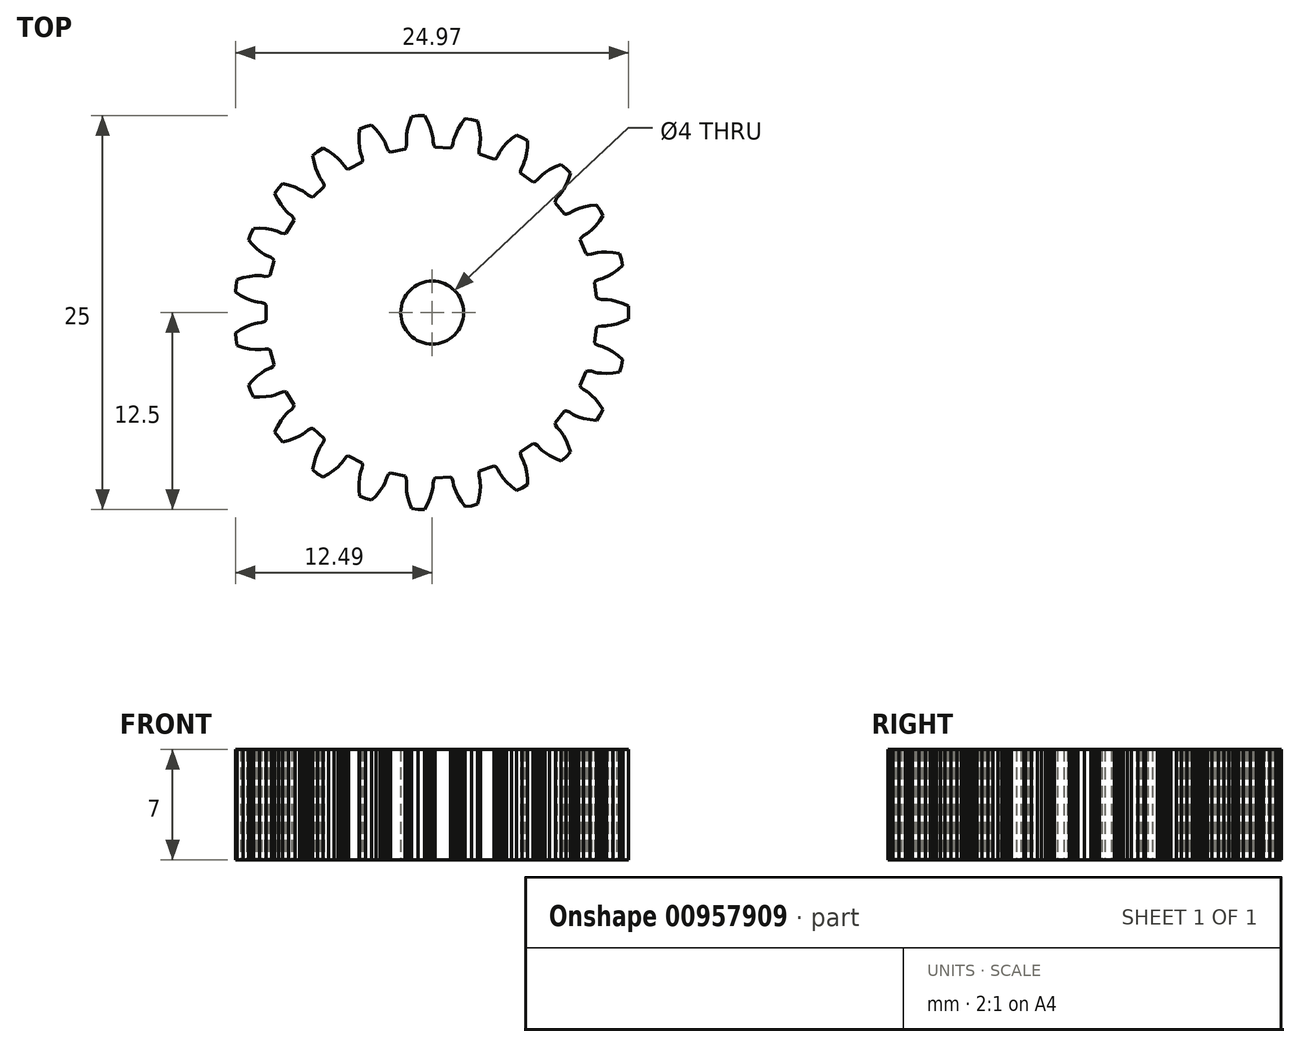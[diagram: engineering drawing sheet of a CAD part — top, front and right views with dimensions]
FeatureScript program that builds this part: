
annotation { "Feature Type Name" : "Feature", "Feature Type Description" : "" }
export const myFeature = defineFeature(function(context is Context, id is Id, definition is map)
    precondition{}
    {
        {
            var Q0;
            Q0=qCreatedBy(makeId("Top.planeOp"),FACE);
            var sketch = newSketch(context, id + "F0", { "sketchPlane" : qUnion([Q0])});
            skLineSegment(sketch, "E0", {"start": v(11.88, -3.76) * mm, "end": v(12.02, -3.38) * mm});
            skLineSegment(sketch, "E1", {"start": v(12.02, -3.38) * mm, "end": v(12.1, -2.98) * mm});
            skLineSegment(sketch, "E2", {"start": v(12.1, -2.98) * mm, "end": v(11.8, -2.73) * mm});
            skLineSegment(sketch, "E3", {"start": v(11.8, -2.73) * mm, "end": v(11.46, -2.48) * mm});
            skLineSegment(sketch, "E4", {"start": v(11.46, -2.48) * mm, "end": v(11.17, -2.32) * mm});
            skLineSegment(sketch, "E5", {"start": v(11.17, -2.32) * mm, "end": v(10.95, -2.22) * mm});
            skLineSegment(sketch, "E6", {"start": v(10.95, -2.22) * mm, "end": v(10.81, -2.17) * mm});
            skLineSegment(sketch, "E7", {"start": v(10.81, -2.17) * mm, "end": v(10.56, -2.1) * mm});
            skLineSegment(sketch, "E8", {"start": v(10.56, -2.1) * mm, "end": v(10.38, -2) * mm});
            skLineSegment(sketch, "E9", {"start": v(10.38, -2) * mm, "end": v(10.3, -1.9) * mm});
            skLineSegment(sketch, "E10", {"start": v(10.3, -1.9) * mm, "end": v(10.42, -0.95) * mm});
            skLineSegment(sketch, "E11", {"start": v(10.42, -0.95) * mm, "end": v(10.53, -0.88) * mm});
            skLineSegment(sketch, "E12", {"start": v(10.53, -0.88) * mm, "end": v(10.74, -0.84) * mm});
            skLineSegment(sketch, "E13", {"start": v(10.74, -0.84) * mm, "end": v(11, -0.85) * mm});
            skLineSegment(sketch, "E14", {"start": v(11, -0.85) * mm, "end": v(11.14, -0.83) * mm});
            skLineSegment(sketch, "E15", {"start": v(11.14, -0.83) * mm, "end": v(11.38, -0.8) * mm});
            skLineSegment(sketch, "E16", {"start": v(11.38, -0.8) * mm, "end": v(11.7, -0.71) * mm});
            skLineSegment(sketch, "E17", {"start": v(11.7, -0.71) * mm, "end": v(12.1, -0.57) * mm});
            skLineSegment(sketch, "E18", {"start": v(12.1, -0.57) * mm, "end": v(12.45, -0.4) * mm});
            skLineSegment(sketch, "E19", {"start": v(12.45, -0.4) * mm, "end": v(12.48, 0) * mm});
            skLineSegment(sketch, "E20", {"start": v(12.48, 0) * mm, "end": v(12.45, 0.4) * mm});
            skLineSegment(sketch, "E21", {"start": v(12.45, 0.4) * mm, "end": v(12.1, 0.57) * mm});
            skLineSegment(sketch, "E22", {"start": v(12.1, 0.57) * mm, "end": v(11.7, 0.71) * mm});
            skLineSegment(sketch, "E23", {"start": v(11.7, 0.71) * mm, "end": v(11.38, 0.8) * mm});
            skLineSegment(sketch, "E24", {"start": v(11.38, 0.8) * mm, "end": v(11.14, 0.83) * mm});
            skLineSegment(sketch, "E25", {"start": v(11.14, 0.83) * mm, "end": v(11, 0.85) * mm});
            skLineSegment(sketch, "E26", {"start": v(11, 0.85) * mm, "end": v(10.74, 0.84) * mm});
            skLineSegment(sketch, "E27", {"start": v(10.74, 0.84) * mm, "end": v(10.53, 0.88) * mm});
            skLineSegment(sketch, "E28", {"start": v(10.53, 0.88) * mm, "end": v(10.42, 0.95) * mm});
            skLineSegment(sketch, "E29", {"start": v(10.42, 0.95) * mm, "end": v(10.3, 1.9) * mm});
            skLineSegment(sketch, "E30", {"start": v(10.3, 1.9) * mm, "end": v(10.38, 2) * mm});
            skLineSegment(sketch, "E31", {"start": v(10.38, 2) * mm, "end": v(10.56, 2.1) * mm});
            skLineSegment(sketch, "E32", {"start": v(10.56, 2.1) * mm, "end": v(10.81, 2.17) * mm});
            skLineSegment(sketch, "E33", {"start": v(10.81, 2.17) * mm, "end": v(10.95, 2.22) * mm});
            skLineSegment(sketch, "E34", {"start": v(10.95, 2.22) * mm, "end": v(11.17, 2.32) * mm});
            skLineSegment(sketch, "E35", {"start": v(11.17, 2.32) * mm, "end": v(11.46, 2.48) * mm});
            skLineSegment(sketch, "E36", {"start": v(11.46, 2.48) * mm, "end": v(11.8, 2.73) * mm});
            skLineSegment(sketch, "E37", {"start": v(11.8, 2.73) * mm, "end": v(12.1, 2.98) * mm});
            skLineSegment(sketch, "E38", {"start": v(12.02, 3.38) * mm, "end": v(11.88, 3.76) * mm});
            skLineSegment(sketch, "E39", {"start": v(11.88, 3.76) * mm, "end": v(11.5, 3.83) * mm});
            skLineSegment(sketch, "E40", {"start": v(11.5, 3.83) * mm, "end": v(11.08, 3.86) * mm});
            skLineSegment(sketch, "E41", {"start": v(11.08, 3.86) * mm, "end": v(10.74, 3.85) * mm});
            skLineSegment(sketch, "E42", {"start": v(10.74, 3.85) * mm, "end": v(10.5, 3.82) * mm});
            skLineSegment(sketch, "E43", {"start": v(10.5, 3.82) * mm, "end": v(10.36, 3.8) * mm});
            skLineSegment(sketch, "E44", {"start": v(10.36, 3.8) * mm, "end": v(10.11, 3.72) * mm});
            skLineSegment(sketch, "E45", {"start": v(10.11, 3.72) * mm, "end": v(9.9, 3.7) * mm});
            skLineSegment(sketch, "E46", {"start": v(9.9, 3.7) * mm, "end": v(9.78, 3.74) * mm});
            skLineSegment(sketch, "E47", {"start": v(9.78, 3.74) * mm, "end": v(9.4, 4.63) * mm});
            skLineSegment(sketch, "E48", {"start": v(9.4, 4.63) * mm, "end": v(9.45, 4.75) * mm});
            skLineSegment(sketch, "E49", {"start": v(9.45, 4.75) * mm, "end": v(9.6, 4.89) * mm});
            skLineSegment(sketch, "E50", {"start": v(9.6, 4.89) * mm, "end": v(9.83, 5.02) * mm});
            skLineSegment(sketch, "E51", {"start": v(9.83, 5.02) * mm, "end": v(9.95, 5.1) * mm});
            skLineSegment(sketch, "E52", {"start": v(9.95, 5.1) * mm, "end": v(10.13, 5.26) * mm});
            skLineSegment(sketch, "E53", {"start": v(10.13, 5.26) * mm, "end": v(10.36, 5.5) * mm});
            skLineSegment(sketch, "E54", {"start": v(10.36, 5.5) * mm, "end": v(10.63, 5.83) * mm});
            skLineSegment(sketch, "E55", {"start": v(10.63, 5.83) * mm, "end": v(10.84, 6.15) * mm});
            skLineSegment(sketch, "E56", {"start": v(10.84, 6.15) * mm, "end": v(10.66, 6.5) * mm});
            skLineSegment(sketch, "E57", {"start": v(10.66, 6.5) * mm, "end": v(10.42, 6.84) * mm});
            skLineSegment(sketch, "E58", {"start": v(10.42, 6.84) * mm, "end": v(10.04, 6.8) * mm});
            skLineSegment(sketch, "E59", {"start": v(10.04, 6.8) * mm, "end": v(9.62, 6.71) * mm});
            skLineSegment(sketch, "E60", {"start": v(9.62, 6.71) * mm, "end": v(9.3, 6.62) * mm});
            skLineSegment(sketch, "E61", {"start": v(9.3, 6.62) * mm, "end": v(9.08, 6.53) * mm});
            skLineSegment(sketch, "E62", {"start": v(9.08, 6.53) * mm, "end": v(8.95, 6.46) * mm});
            skLineSegment(sketch, "E63", {"start": v(8.95, 6.46) * mm, "end": v(8.73, 6.32) * mm});
            skLineSegment(sketch, "E64", {"start": v(8.73, 6.32) * mm, "end": v(8.53, 6.25) * mm});
            skLineSegment(sketch, "E65", {"start": v(8.53, 6.25) * mm, "end": v(8.4, 6.26) * mm});
            skLineSegment(sketch, "E66", {"start": v(8.4, 6.26) * mm, "end": v(7.8, 7) * mm});
            skLineSegment(sketch, "E67", {"start": v(7.8, 7) * mm, "end": v(7.82, 7.13) * mm});
            skLineSegment(sketch, "E68", {"start": v(7.82, 7.13) * mm, "end": v(7.93, 7.3) * mm});
            skLineSegment(sketch, "E69", {"start": v(7.93, 7.3) * mm, "end": v(8.1, 7.5) * mm});
            skLineSegment(sketch, "E70", {"start": v(8.1, 7.5) * mm, "end": v(8.2, 7.6) * mm});
            skLineSegment(sketch, "E71", {"start": v(8.2, 7.6) * mm, "end": v(8.34, 7.81) * mm});
            skLineSegment(sketch, "E72", {"start": v(8.34, 7.81) * mm, "end": v(8.5, 8.1) * mm});
            skLineSegment(sketch, "E73", {"start": v(8.5, 8.1) * mm, "end": v(8.66, 8.5) * mm});
            skLineSegment(sketch, "E74", {"start": v(8.66, 8.5) * mm, "end": v(8.78, 8.86) * mm});
            skLineSegment(sketch, "E75", {"start": v(8.78, 8.86) * mm, "end": v(8.5, 9.16) * mm});
            skLineSegment(sketch, "E76", {"start": v(8.5, 9.16) * mm, "end": v(8.19, 9.41) * mm});
            skLineSegment(sketch, "E77", {"start": v(8.19, 9.41) * mm, "end": v(7.83, 9.27) * mm});
            skLineSegment(sketch, "E78", {"start": v(7.83, 9.27) * mm, "end": v(7.45, 9.07) * mm});
            skLineSegment(sketch, "E79", {"start": v(7.45, 9.07) * mm, "end": v(7.17, 8.9) * mm});
            skLineSegment(sketch, "E80", {"start": v(7.17, 8.9) * mm, "end": v(6.98, 8.75) * mm});
            skLineSegment(sketch, "E81", {"start": v(6.98, 8.75) * mm, "end": v(6.87, 8.65) * mm});
            skLineSegment(sketch, "E82", {"start": v(6.87, 8.65) * mm, "end": v(6.7, 8.46) * mm});
            skLineSegment(sketch, "E83", {"start": v(6.7, 8.46) * mm, "end": v(6.53, 8.33) * mm});
            skLineSegment(sketch, "E84", {"start": v(6.53, 8.33) * mm, "end": v(6.4, 8.3) * mm});
            skLineSegment(sketch, "E85", {"start": v(6.4, 8.3) * mm, "end": v(5.62, 8.86) * mm});
            skLineSegment(sketch, "E86", {"start": v(5.62, 8.86) * mm, "end": v(5.6, 8.99) * mm});
            skLineSegment(sketch, "E87", {"start": v(5.6, 8.99) * mm, "end": v(5.66, 9.19) * mm});
            skLineSegment(sketch, "E88", {"start": v(5.66, 9.19) * mm, "end": v(5.78, 9.42) * mm});
            skLineSegment(sketch, "E89", {"start": v(5.78, 9.42) * mm, "end": v(5.84, 9.55) * mm});
            skLineSegment(sketch, "E90", {"start": v(5.84, 9.55) * mm, "end": v(5.92, 9.78) * mm});
            skLineSegment(sketch, "E91", {"start": v(5.92, 9.78) * mm, "end": v(6, 10.1) * mm});
            skLineSegment(sketch, "E92", {"start": v(6, 10.1) * mm, "end": v(6.05, 10.53) * mm});
            skLineSegment(sketch, "E93", {"start": v(6.05, 10.53) * mm, "end": v(6.06, 10.91) * mm});
            skLineSegment(sketch, "E94", {"start": v(6.06, 10.91) * mm, "end": v(5.72, 11.12) * mm});
            skLineSegment(sketch, "E95", {"start": v(5.72, 11.12) * mm, "end": v(5.34, 11.29) * mm});
            skLineSegment(sketch, "E96", {"start": v(5.34, 11.29) * mm, "end": v(5.04, 11.05) * mm});
            skLineSegment(sketch, "E97", {"start": v(5.04, 11.05) * mm, "end": v(4.73, 10.76) * mm});
            skLineSegment(sketch, "E98", {"start": v(4.73, 10.76) * mm, "end": v(4.5, 10.51) * mm});
            skLineSegment(sketch, "E99", {"start": v(4.5, 10.51) * mm, "end": v(4.36, 10.32) * mm});
            skLineSegment(sketch, "E100", {"start": v(4.36, 10.32) * mm, "end": v(4.28, 10.2) * mm});
            skLineSegment(sketch, "E101", {"start": v(4.28, 10.2) * mm, "end": v(4.17, 9.96) * mm});
            skLineSegment(sketch, "E102", {"start": v(4.17, 9.96) * mm, "end": v(4.04, 9.8) * mm});
            skLineSegment(sketch, "E103", {"start": v(4.04, 9.8) * mm, "end": v(3.92, 9.74) * mm});
            skLineSegment(sketch, "E104", {"start": v(3.92, 9.74) * mm, "end": v(3.02, 10.06) * mm});
            skLineSegment(sketch, "E105", {"start": v(3.02, 10.06) * mm, "end": v(2.97, 10.18) * mm});
            skLineSegment(sketch, "E106", {"start": v(2.97, 10.18) * mm, "end": v(2.97, 10.39) * mm});
            skLineSegment(sketch, "E107", {"start": v(2.97, 10.39) * mm, "end": v(3.03, 10.64) * mm});
            skLineSegment(sketch, "E108", {"start": v(3.03, 10.64) * mm, "end": v(3.05, 10.79) * mm});
            skLineSegment(sketch, "E109", {"start": v(3.05, 10.79) * mm, "end": v(3.06, 11.03) * mm});
            skLineSegment(sketch, "E110", {"start": v(3.06, 11.03) * mm, "end": v(3.04, 11.36) * mm});
            skLineSegment(sketch, "E111", {"start": v(3.04, 11.36) * mm, "end": v(2.98, 11.78) * mm});
            skLineSegment(sketch, "E112", {"start": v(2.98, 11.78) * mm, "end": v(2.9, 12.16) * mm});
            skLineSegment(sketch, "E113", {"start": v(2.9, 12.16) * mm, "end": v(2.5, 12.27) * mm});
            skLineSegment(sketch, "E114", {"start": v(2.5, 12.27) * mm, "end": v(2.1, 12.32) * mm});
            skLineSegment(sketch, "E115", {"start": v(2.1, 12.32) * mm, "end": v(1.87, 12.01) * mm});
            skLineSegment(sketch, "E116", {"start": v(1.87, 12.01) * mm, "end": v(1.65, 11.65) * mm});
            skLineSegment(sketch, "E117", {"start": v(1.65, 11.65) * mm, "end": v(1.5, 11.35) * mm});
            skLineSegment(sketch, "E118", {"start": v(1.5, 11.35) * mm, "end": v(1.41, 11.13) * mm});
            skLineSegment(sketch, "E119", {"start": v(1.41, 11.13) * mm, "end": v(1.37, 10.98) * mm});
            skLineSegment(sketch, "E120", {"start": v(1.37, 10.98) * mm, "end": v(1.32, 10.73) * mm});
            skLineSegment(sketch, "E121", {"start": v(1.32, 10.73) * mm, "end": v(1.24, 10.54) * mm});
            skLineSegment(sketch, "E122", {"start": v(1.24, 10.54) * mm, "end": v(1.15, 10.45) * mm});
            skLineSegment(sketch, "E123", {"start": v(1.15, 10.45) * mm, "end": v(0.19, 10.51) * mm});
            skLineSegment(sketch, "E124", {"start": v(0.19, 10.51) * mm, "end": v(0.1, 10.61) * mm});
            skLineSegment(sketch, "E125", {"start": v(0.1, 10.61) * mm, "end": v(0.05, 10.82) * mm});
            skLineSegment(sketch, "E126", {"start": v(0.05, 10.82) * mm, "end": v(0.04, 11.08) * mm});
            skLineSegment(sketch, "E127", {"start": v(0.04, 11.08) * mm, "end": v(0.02, 11.22) * mm});
            skLineSegment(sketch, "E128", {"start": v(0.02, 11.22) * mm, "end": v(-0.03, 11.46) * mm});
            skLineSegment(sketch, "E129", {"start": v(-0.03, 11.46) * mm, "end": v(-0.14, 11.77) * mm});
            skLineSegment(sketch, "E130", {"start": v(-0.14, 11.77) * mm, "end": v(-0.3, 12.16) * mm});
            skLineSegment(sketch, "E131", {"start": v(-0.3, 12.16) * mm, "end": v(-0.5, 12.5) * mm});
            skLineSegment(sketch, "E132", {"start": v(-0.5, 12.5) * mm, "end": v(-0.9, 12.5) * mm});
            skLineSegment(sketch, "E133", {"start": v(-0.9, 12.5) * mm, "end": v(-1.3, 12.44) * mm});
            skLineSegment(sketch, "E134", {"start": v(-1.3, 12.44) * mm, "end": v(-1.44, 12.08) * mm});
            skLineSegment(sketch, "E135", {"start": v(-1.44, 12.08) * mm, "end": v(-1.56, 11.67) * mm});
            skLineSegment(sketch, "E136", {"start": v(-1.56, 11.67) * mm, "end": v(-1.62, 11.35) * mm});
            skLineSegment(sketch, "E137", {"start": v(-1.62, 11.35) * mm, "end": v(-1.64, 11.1) * mm});
            skLineSegment(sketch, "E138", {"start": v(-1.64, 11.1) * mm, "end": v(-1.64, 10.96) * mm});
            skLineSegment(sketch, "E139", {"start": v(-1.64, 10.96) * mm, "end": v(-1.62, 10.7) * mm});
            skLineSegment(sketch, "E140", {"start": v(-1.62, 10.7) * mm, "end": v(-1.65, 10.5) * mm});
            skLineSegment(sketch, "E141", {"start": v(-1.65, 10.5) * mm, "end": v(-1.71, 10.38) * mm});
            skLineSegment(sketch, "E142", {"start": v(-1.71, 10.38) * mm, "end": v(-2.66, 10.19) * mm});
            skLineSegment(sketch, "E143", {"start": v(-2.66, 10.19) * mm, "end": v(-2.76, 10.26) * mm});
            skLineSegment(sketch, "E144", {"start": v(-2.76, 10.26) * mm, "end": v(-2.87, 10.44) * mm});
            skLineSegment(sketch, "E145", {"start": v(-2.87, 10.44) * mm, "end": v(-2.95, 10.69) * mm});
            skLineSegment(sketch, "E146", {"start": v(-2.95, 10.69) * mm, "end": v(-3, 10.83) * mm});
            skLineSegment(sketch, "E147", {"start": v(-3, 10.83) * mm, "end": v(-3.13, 11.04) * mm});
            skLineSegment(sketch, "E148", {"start": v(-3.13, 11.04) * mm, "end": v(-3.31, 11.31) * mm});
            skLineSegment(sketch, "E149", {"start": v(-3.31, 11.31) * mm, "end": v(-3.58, 11.64) * mm});
            skLineSegment(sketch, "E150", {"start": v(-3.58, 11.64) * mm, "end": v(-3.85, 11.92) * mm});
            skLineSegment(sketch, "E151", {"start": v(-3.85, 11.92) * mm, "end": v(-4.24, 11.8) * mm});
            skLineSegment(sketch, "E152", {"start": v(-4.24, 11.8) * mm, "end": v(-4.62, 11.64) * mm});
            skLineSegment(sketch, "E153", {"start": v(-4.62, 11.64) * mm, "end": v(-4.65, 11.26) * mm});
            skLineSegment(sketch, "E154", {"start": v(-4.65, 11.26) * mm, "end": v(-4.65, 10.83) * mm});
            skLineSegment(sketch, "E155", {"start": v(-4.65, 10.83) * mm, "end": v(-4.62, 10.5) * mm});
            skLineSegment(sketch, "E156", {"start": v(-4.62, 10.5) * mm, "end": v(-4.58, 10.27) * mm});
            skLineSegment(sketch, "E157", {"start": v(-4.58, 10.27) * mm, "end": v(-4.54, 10.12) * mm});
            skLineSegment(sketch, "E158", {"start": v(-4.54, 10.12) * mm, "end": v(-4.45, 9.88) * mm});
            skLineSegment(sketch, "E159", {"start": v(-4.45, 9.88) * mm, "end": v(-4.42, 9.67) * mm});
            skLineSegment(sketch, "E160", {"start": v(-4.42, 9.67) * mm, "end": v(-4.45, 9.55) * mm});
            skLineSegment(sketch, "E161", {"start": v(-4.45, 9.55) * mm, "end": v(-5.3, 9.1) * mm});
            skLineSegment(sketch, "E162", {"start": v(-5.3, 9.1) * mm, "end": v(-5.43, 9.15) * mm});
            skLineSegment(sketch, "E163", {"start": v(-5.43, 9.15) * mm, "end": v(-5.58, 9.3) * mm});
            skLineSegment(sketch, "E164", {"start": v(-5.58, 9.3) * mm, "end": v(-5.73, 9.5) * mm});
            skLineSegment(sketch, "E165", {"start": v(-5.73, 9.5) * mm, "end": v(-5.82, 9.62) * mm});
            skLineSegment(sketch, "E166", {"start": v(-5.82, 9.62) * mm, "end": v(-5.99, 9.8) * mm});
            skLineSegment(sketch, "E167", {"start": v(-5.99, 9.8) * mm, "end": v(-6.24, 10.01) * mm});
            skLineSegment(sketch, "E168", {"start": v(-6.24, 10.01) * mm, "end": v(-6.59, 10.25) * mm});
            skLineSegment(sketch, "E169", {"start": v(-6.59, 10.25) * mm, "end": v(-6.93, 10.45) * mm});
            skLineSegment(sketch, "E170", {"start": v(-6.93, 10.45) * mm, "end": v(-7.27, 10.24) * mm});
            skLineSegment(sketch, "E171", {"start": v(-7.27, 10.24) * mm, "end": v(-7.59, 9.98) * mm});
            skLineSegment(sketch, "E172", {"start": v(-7.59, 9.98) * mm, "end": v(-7.52, 9.6) * mm});
            skLineSegment(sketch, "E173", {"start": v(-7.52, 9.6) * mm, "end": v(-7.4, 9.19) * mm});
            skLineSegment(sketch, "E174", {"start": v(-7.4, 9.19) * mm, "end": v(-7.29, 8.88) * mm});
            skLineSegment(sketch, "E175", {"start": v(-7.29, 8.88) * mm, "end": v(-7.18, 8.66) * mm});
            skLineSegment(sketch, "E176", {"start": v(-7.18, 8.66) * mm, "end": v(-7.1, 8.53) * mm});
            skLineSegment(sketch, "E177", {"start": v(-7.1, 8.53) * mm, "end": v(-6.95, 8.33) * mm});
            skLineSegment(sketch, "E178", {"start": v(-6.95, 8.33) * mm, "end": v(-6.87, 8.14) * mm});
            skLineSegment(sketch, "E179", {"start": v(-6.87, 8.14) * mm, "end": v(-6.87, 8) * mm});
            skLineSegment(sketch, "E180", {"start": v(-6.87, 8) * mm, "end": v(-7.57, 7.35) * mm});
            skLineSegment(sketch, "E181", {"start": v(-7.57, 7.35) * mm, "end": v(-7.7, 7.36) * mm});
            skLineSegment(sketch, "E182", {"start": v(-7.7, 7.36) * mm, "end": v(-7.88, 7.46) * mm});
            skLineSegment(sketch, "E183", {"start": v(-7.88, 7.46) * mm, "end": v(-8.08, 7.63) * mm});
            skLineSegment(sketch, "E184", {"start": v(-8.08, 7.63) * mm, "end": v(-8.2, 7.71) * mm});
            skLineSegment(sketch, "E185", {"start": v(-8.2, 7.71) * mm, "end": v(-8.41, 7.83) * mm});
            skLineSegment(sketch, "E186", {"start": v(-8.41, 7.83) * mm, "end": v(-8.71, 7.97) * mm});
            skLineSegment(sketch, "E187", {"start": v(-8.71, 7.97) * mm, "end": v(-9.11, 8.1) * mm});
            skLineSegment(sketch, "E188", {"start": v(-9.11, 8.1) * mm, "end": v(-9.49, 8.2) * mm});
            skLineSegment(sketch, "E189", {"start": v(-9.49, 8.2) * mm, "end": v(-9.77, 7.9) * mm});
            skLineSegment(sketch, "E190", {"start": v(-9.77, 7.9) * mm, "end": v(-10, 7.58) * mm});
            skLineSegment(sketch, "E191", {"start": v(-10, 7.58) * mm, "end": v(-9.83, 7.23) * mm});
            skLineSegment(sketch, "E192", {"start": v(-9.83, 7.23) * mm, "end": v(-9.61, 6.86) * mm});
            skLineSegment(sketch, "E193", {"start": v(-9.61, 6.86) * mm, "end": v(-9.42, 6.6) * mm});
            skLineSegment(sketch, "E194", {"start": v(-9.42, 6.6) * mm, "end": v(-9.26, 6.42) * mm});
            skLineSegment(sketch, "E195", {"start": v(-9.26, 6.42) * mm, "end": v(-9.15, 6.31) * mm});
            skLineSegment(sketch, "E196", {"start": v(-9.15, 6.31) * mm, "end": v(-8.94, 6.15) * mm});
            skLineSegment(sketch, "E197", {"start": v(-8.94, 6.15) * mm, "end": v(-8.8, 6) * mm});
            skLineSegment(sketch, "E198", {"start": v(-8.8, 6) * mm, "end": v(-8.77, 5.87) * mm});
            skLineSegment(sketch, "E199", {"start": v(-8.77, 5.87) * mm, "end": v(-9.27, 5.05) * mm});
            skLineSegment(sketch, "E200", {"start": v(-9.27, 5.05) * mm, "end": v(-9.4, 5.02) * mm});
            skLineSegment(sketch, "E201", {"start": v(-9.4, 5.02) * mm, "end": v(-9.6, 5.07) * mm});
            skLineSegment(sketch, "E202", {"start": v(-9.6, 5.07) * mm, "end": v(-9.84, 5.18) * mm});
            skLineSegment(sketch, "E203", {"start": v(-9.84, 5.18) * mm, "end": v(-9.98, 5.22) * mm});
            skLineSegment(sketch, "E204", {"start": v(-9.98, 5.22) * mm, "end": v(-10.21, 5.28) * mm});
            skLineSegment(sketch, "E205", {"start": v(-10.21, 5.28) * mm, "end": v(-10.54, 5.33) * mm});
            skLineSegment(sketch, "E206", {"start": v(-10.54, 5.33) * mm, "end": v(-10.96, 5.36) * mm});
            skLineSegment(sketch, "E207", {"start": v(-10.96, 5.36) * mm, "end": v(-11.35, 5.35) * mm});
            skLineSegment(sketch, "E208", {"start": v(-11.35, 5.35) * mm, "end": v(-11.54, 5) * mm});
            skLineSegment(sketch, "E209", {"start": v(-11.54, 5) * mm, "end": v(-11.68, 4.6) * mm});
            skLineSegment(sketch, "E210", {"start": v(-11.68, 4.6) * mm, "end": v(-11.42, 4.32) * mm});
            skLineSegment(sketch, "E211", {"start": v(-11.42, 4.32) * mm, "end": v(-11.1, 4.03) * mm});
            skLineSegment(sketch, "E212", {"start": v(-11.1, 4.03) * mm, "end": v(-10.85, 3.82) * mm});
            skLineSegment(sketch, "E213", {"start": v(-10.85, 3.82) * mm, "end": v(-10.65, 3.7) * mm});
            skLineSegment(sketch, "E214", {"start": v(-10.65, 3.7) * mm, "end": v(-10.51, 3.62) * mm});
            skLineSegment(sketch, "E215", {"start": v(-10.51, 3.62) * mm, "end": v(-10.27, 3.53) * mm});
            skLineSegment(sketch, "E216", {"start": v(-10.27, 3.53) * mm, "end": v(-10.1, 3.4) * mm});
            skLineSegment(sketch, "E217", {"start": v(-10.1, 3.4) * mm, "end": v(-10.03, 3.3) * mm});
            skLineSegment(sketch, "E218", {"start": v(-10.03, 3.3) * mm, "end": v(-10.3, 2.37) * mm});
            skLineSegment(sketch, "E219", {"start": v(-10.3, 2.37) * mm, "end": v(-10.4, 2.31) * mm});
            skLineSegment(sketch, "E220", {"start": v(-10.4, 2.31) * mm, "end": v(-10.62, 2.3) * mm});
            skLineSegment(sketch, "E221", {"start": v(-10.62, 2.3) * mm, "end": v(-10.87, 2.34) * mm});
            skLineSegment(sketch, "E222", {"start": v(-10.87, 2.34) * mm, "end": v(-11.02, 2.35) * mm});
            skLineSegment(sketch, "E223", {"start": v(-11.02, 2.35) * mm, "end": v(-11.26, 2.34) * mm});
            skLineSegment(sketch, "E224", {"start": v(-11.26, 2.34) * mm, "end": v(-11.6, 2.3) * mm});
            skLineSegment(sketch, "E225", {"start": v(-11.6, 2.3) * mm, "end": v(-12, 2.22) * mm});
            skLineSegment(sketch, "E226", {"start": v(-12, 2.22) * mm, "end": v(-12.38, 2.1) * mm});
            skLineSegment(sketch, "E227", {"start": v(-12.38, 2.1) * mm, "end": v(-12.46, 1.7) * mm});
            skLineSegment(sketch, "E228", {"start": v(-12.46, 1.7) * mm, "end": v(-12.49, 1.3) * mm});
            skLineSegment(sketch, "E229", {"start": v(-12.49, 1.3) * mm, "end": v(-12.16, 1.1) * mm});
            skLineSegment(sketch, "E230", {"start": v(-12.16, 1.1) * mm, "end": v(-11.79, 0.9) * mm});
            skLineSegment(sketch, "E231", {"start": v(-11.79, 0.9) * mm, "end": v(-11.48, 0.77) * mm});
            skLineSegment(sketch, "E232", {"start": v(-11.48, 0.77) * mm, "end": v(-11.25, 0.7) * mm});
            skLineSegment(sketch, "E233", {"start": v(-11.25, 0.7) * mm, "end": v(-11.1, 0.67) * mm});
            skLineSegment(sketch, "E234", {"start": v(-11.1, 0.67) * mm, "end": v(-10.85, 0.64) * mm});
            skLineSegment(sketch, "E235", {"start": v(-10.85, 0.64) * mm, "end": v(-10.65, 0.57) * mm});
            skLineSegment(sketch, "E236", {"start": v(-10.65, 0.57) * mm, "end": v(-10.55, 0.48) * mm});
            skLineSegment(sketch, "E237", {"start": v(-10.55, 0.48) * mm, "end": v(-10.55, -0.48) * mm});
            skLineSegment(sketch, "E238", {"start": v(-10.55, -0.48) * mm, "end": v(-10.65, -0.57) * mm});
            skLineSegment(sketch, "E239", {"start": v(-10.65, -0.57) * mm, "end": v(-10.85, -0.64) * mm});
            skLineSegment(sketch, "E240", {"start": v(-10.85, -0.64) * mm, "end": v(-11.1, -0.67) * mm});
            skLineSegment(sketch, "E241", {"start": v(-11.1, -0.67) * mm, "end": v(-11.25, -0.7) * mm});
            skLineSegment(sketch, "E242", {"start": v(-11.25, -0.7) * mm, "end": v(-11.48, -0.77) * mm});
            skLineSegment(sketch, "E243", {"start": v(-11.48, -0.77) * mm, "end": v(-11.79, -0.9) * mm});
            skLineSegment(sketch, "E244", {"start": v(-11.79, -0.9) * mm, "end": v(-12.16, -1.1) * mm});
            skLineSegment(sketch, "E245", {"start": v(-12.16, -1.1) * mm, "end": v(-12.49, -1.3) * mm});
            skLineSegment(sketch, "E246", {"start": v(-12.49, -1.3) * mm, "end": v(-12.46, -1.7) * mm});
            skLineSegment(sketch, "E247", {"start": v(-12.46, -1.7) * mm, "end": v(-12.38, -2.1) * mm});
            skLineSegment(sketch, "E248", {"start": v(-12.38, -2.1) * mm, "end": v(-12, -2.22) * mm});
            skLineSegment(sketch, "E249", {"start": v(-12, -2.22) * mm, "end": v(-11.6, -2.3) * mm});
            skLineSegment(sketch, "E250", {"start": v(-11.6, -2.3) * mm, "end": v(-11.26, -2.34) * mm});
            skLineSegment(sketch, "E251", {"start": v(-11.26, -2.34) * mm, "end": v(-11.02, -2.35) * mm});
            skLineSegment(sketch, "E252", {"start": v(-11.02, -2.35) * mm, "end": v(-10.87, -2.34) * mm});
            skLineSegment(sketch, "E253", {"start": v(-10.87, -2.34) * mm, "end": v(-10.62, -2.3) * mm});
            skLineSegment(sketch, "E254", {"start": v(-10.62, -2.3) * mm, "end": v(-10.4, -2.31) * mm});
            skLineSegment(sketch, "E255", {"start": v(-10.4, -2.31) * mm, "end": v(-10.3, -2.37) * mm});
            skLineSegment(sketch, "E256", {"start": v(-10.3, -2.37) * mm, "end": v(-10.03, -3.3) * mm});
            skLineSegment(sketch, "E257", {"start": v(-10.03, -3.3) * mm, "end": v(-10.1, -3.4) * mm});
            skLineSegment(sketch, "E258", {"start": v(-10.1, -3.4) * mm, "end": v(-10.27, -3.53) * mm});
            skLineSegment(sketch, "E259", {"start": v(-10.27, -3.53) * mm, "end": v(-10.51, -3.62) * mm});
            skLineSegment(sketch, "E260", {"start": v(-10.51, -3.62) * mm, "end": v(-10.65, -3.7) * mm});
            skLineSegment(sketch, "E261", {"start": v(-10.65, -3.7) * mm, "end": v(-10.85, -3.82) * mm});
            skLineSegment(sketch, "E262", {"start": v(-10.85, -3.82) * mm, "end": v(-11.1, -4.03) * mm});
            skLineSegment(sketch, "E263", {"start": v(-11.1, -4.03) * mm, "end": v(-11.42, -4.32) * mm});
            skLineSegment(sketch, "E264", {"start": v(-11.42, -4.32) * mm, "end": v(-11.68, -4.6) * mm});
            skLineSegment(sketch, "E265", {"start": v(-11.68, -4.6) * mm, "end": v(-11.54, -5) * mm});
            skLineSegment(sketch, "E266", {"start": v(-11.54, -5) * mm, "end": v(-11.35, -5.35) * mm});
            skLineSegment(sketch, "E267", {"start": v(-11.35, -5.35) * mm, "end": v(-10.96, -5.36) * mm});
            skLineSegment(sketch, "E268", {"start": v(-10.96, -5.36) * mm, "end": v(-10.54, -5.33) * mm});
            skLineSegment(sketch, "E269", {"start": v(-10.54, -5.33) * mm, "end": v(-10.21, -5.28) * mm});
            skLineSegment(sketch, "E270", {"start": v(-10.21, -5.28) * mm, "end": v(-9.98, -5.22) * mm});
            skLineSegment(sketch, "E271", {"start": v(-9.98, -5.22) * mm, "end": v(-9.84, -5.18) * mm});
            skLineSegment(sketch, "E272", {"start": v(-9.84, -5.18) * mm, "end": v(-9.6, -5.07) * mm});
            skLineSegment(sketch, "E273", {"start": v(-9.6, -5.07) * mm, "end": v(-9.4, -5.02) * mm});
            skLineSegment(sketch, "E274", {"start": v(-9.4, -5.02) * mm, "end": v(-9.27, -5.05) * mm});
            skLineSegment(sketch, "E275", {"start": v(-9.27, -5.05) * mm, "end": v(-8.77, -5.87) * mm});
            skLineSegment(sketch, "E276", {"start": v(-8.77, -5.87) * mm, "end": v(-8.8, -6) * mm});
            skLineSegment(sketch, "E277", {"start": v(-8.8, -6) * mm, "end": v(-8.94, -6.15) * mm});
            skLineSegment(sketch, "E278", {"start": v(-8.94, -6.15) * mm, "end": v(-9.15, -6.31) * mm});
            skLineSegment(sketch, "E279", {"start": v(-9.15, -6.31) * mm, "end": v(-9.26, -6.42) * mm});
            skLineSegment(sketch, "E280", {"start": v(-9.26, -6.42) * mm, "end": v(-9.42, -6.6) * mm});
            skLineSegment(sketch, "E281", {"start": v(-9.42, -6.6) * mm, "end": v(-9.61, -6.86) * mm});
            skLineSegment(sketch, "E282", {"start": v(-9.61, -6.86) * mm, "end": v(-9.83, -7.23) * mm});
            skLineSegment(sketch, "E283", {"start": v(-9.83, -7.23) * mm, "end": v(-10, -7.58) * mm});
            skLineSegment(sketch, "E284", {"start": v(-10, -7.58) * mm, "end": v(-9.77, -7.9) * mm});
            skLineSegment(sketch, "E285", {"start": v(-9.77, -7.9) * mm, "end": v(-9.49, -8.2) * mm});
            skLineSegment(sketch, "E286", {"start": v(-9.49, -8.2) * mm, "end": v(-9.11, -8.1) * mm});
            skLineSegment(sketch, "E287", {"start": v(-9.11, -8.1) * mm, "end": v(-8.71, -7.97) * mm});
            skLineSegment(sketch, "E288", {"start": v(-8.71, -7.97) * mm, "end": v(-8.41, -7.83) * mm});
            skLineSegment(sketch, "E289", {"start": v(-8.41, -7.83) * mm, "end": v(-8.2, -7.71) * mm});
            skLineSegment(sketch, "E290", {"start": v(-8.2, -7.71) * mm, "end": v(-8.08, -7.63) * mm});
            skLineSegment(sketch, "E291", {"start": v(-8.08, -7.63) * mm, "end": v(-7.88, -7.46) * mm});
            skLineSegment(sketch, "E292", {"start": v(-7.88, -7.46) * mm, "end": v(-7.7, -7.36) * mm});
            skLineSegment(sketch, "E293", {"start": v(-7.7, -7.36) * mm, "end": v(-7.57, -7.35) * mm});
            skLineSegment(sketch, "E294", {"start": v(-7.57, -7.35) * mm, "end": v(-6.87, -8) * mm});
            skLineSegment(sketch, "E295", {"start": v(-6.87, -8) * mm, "end": v(-6.87, -8.14) * mm});
            skLineSegment(sketch, "E296", {"start": v(-6.87, -8.14) * mm, "end": v(-6.95, -8.33) * mm});
            skLineSegment(sketch, "E297", {"start": v(-6.95, -8.33) * mm, "end": v(-7.1, -8.53) * mm});
            skLineSegment(sketch, "E298", {"start": v(-7.1, -8.53) * mm, "end": v(-7.18, -8.66) * mm});
            skLineSegment(sketch, "E299", {"start": v(-7.18, -8.66) * mm, "end": v(-7.29, -8.88) * mm});
            skLineSegment(sketch, "E300", {"start": v(-7.29, -8.88) * mm, "end": v(-7.4, -9.19) * mm});
            skLineSegment(sketch, "E301", {"start": v(-7.4, -9.19) * mm, "end": v(-7.52, -9.6) * mm});
            skLineSegment(sketch, "E302", {"start": v(-7.52, -9.6) * mm, "end": v(-7.59, -9.98) * mm});
            skLineSegment(sketch, "E303", {"start": v(-7.59, -9.98) * mm, "end": v(-7.27, -10.24) * mm});
            skLineSegment(sketch, "E304", {"start": v(-7.27, -10.24) * mm, "end": v(-6.93, -10.45) * mm});
            skLineSegment(sketch, "E305", {"start": v(-6.93, -10.45) * mm, "end": v(-6.59, -10.25) * mm});
            skLineSegment(sketch, "E306", {"start": v(-6.59, -10.25) * mm, "end": v(-6.24, -10.01) * mm});
            skLineSegment(sketch, "E307", {"start": v(-6.24, -10.01) * mm, "end": v(-5.99, -9.8) * mm});
            skLineSegment(sketch, "E308", {"start": v(-5.99, -9.8) * mm, "end": v(-5.82, -9.62) * mm});
            skLineSegment(sketch, "E309", {"start": v(-5.82, -9.62) * mm, "end": v(-5.73, -9.5) * mm});
            skLineSegment(sketch, "E310", {"start": v(-5.73, -9.5) * mm, "end": v(-5.58, -9.3) * mm});
            skLineSegment(sketch, "E311", {"start": v(-5.58, -9.3) * mm, "end": v(-5.43, -9.15) * mm});
            skLineSegment(sketch, "E312", {"start": v(-5.43, -9.15) * mm, "end": v(-5.3, -9.1) * mm});
            skLineSegment(sketch, "E313", {"start": v(-5.3, -9.1) * mm, "end": v(-4.45, -9.55) * mm});
            skLineSegment(sketch, "E314", {"start": v(-4.45, -9.55) * mm, "end": v(-4.42, -9.67) * mm});
            skLineSegment(sketch, "E315", {"start": v(-4.42, -9.67) * mm, "end": v(-4.45, -9.88) * mm});
            skLineSegment(sketch, "E316", {"start": v(-4.45, -9.88) * mm, "end": v(-4.54, -10.12) * mm});
            skLineSegment(sketch, "E317", {"start": v(-4.54, -10.12) * mm, "end": v(-4.58, -10.27) * mm});
            skLineSegment(sketch, "E318", {"start": v(-4.58, -10.27) * mm, "end": v(-4.62, -10.5) * mm});
            skLineSegment(sketch, "E319", {"start": v(-4.62, -10.5) * mm, "end": v(-4.65, -10.83) * mm});
            skLineSegment(sketch, "E320", {"start": v(-4.65, -10.83) * mm, "end": v(-4.65, -11.26) * mm});
            skLineSegment(sketch, "E321", {"start": v(-4.65, -11.26) * mm, "end": v(-4.62, -11.64) * mm});
            skLineSegment(sketch, "E322", {"start": v(-4.62, -11.64) * mm, "end": v(-4.24, -11.8) * mm});
            skLineSegment(sketch, "E323", {"start": v(-4.24, -11.8) * mm, "end": v(-3.85, -11.92) * mm});
            skLineSegment(sketch, "E324", {"start": v(-3.85, -11.92) * mm, "end": v(-3.58, -11.64) * mm});
            skLineSegment(sketch, "E325", {"start": v(-3.58, -11.64) * mm, "end": v(-3.31, -11.31) * mm});
            skLineSegment(sketch, "E326", {"start": v(-3.31, -11.31) * mm, "end": v(-3.13, -11.04) * mm});
            skLineSegment(sketch, "E327", {"start": v(-3.13, -11.04) * mm, "end": v(-3, -10.83) * mm});
            skLineSegment(sketch, "E328", {"start": v(-3, -10.83) * mm, "end": v(-2.95, -10.69) * mm});
            skLineSegment(sketch, "E329", {"start": v(-2.95, -10.69) * mm, "end": v(-2.87, -10.44) * mm});
            skLineSegment(sketch, "E330", {"start": v(-2.87, -10.44) * mm, "end": v(-2.76, -10.26) * mm});
            skLineSegment(sketch, "E331", {"start": v(-2.76, -10.26) * mm, "end": v(-2.66, -10.19) * mm});
            skLineSegment(sketch, "E332", {"start": v(-2.66, -10.19) * mm, "end": v(-1.71, -10.38) * mm});
            skLineSegment(sketch, "E333", {"start": v(-1.71, -10.38) * mm, "end": v(-1.65, -10.5) * mm});
            skLineSegment(sketch, "E334", {"start": v(-1.65, -10.5) * mm, "end": v(-1.62, -10.7) * mm});
            skLineSegment(sketch, "E335", {"start": v(-1.62, -10.7) * mm, "end": v(-1.64, -10.96) * mm});
            skLineSegment(sketch, "E336", {"start": v(-1.64, -10.96) * mm, "end": v(-1.64, -11.1) * mm});
            skLineSegment(sketch, "E337", {"start": v(-1.64, -11.1) * mm, "end": v(-1.62, -11.35) * mm});
            skLineSegment(sketch, "E338", {"start": v(-1.62, -11.35) * mm, "end": v(-1.56, -11.67) * mm});
            skLineSegment(sketch, "E339", {"start": v(-1.56, -11.67) * mm, "end": v(-1.44, -12.08) * mm});
            skLineSegment(sketch, "E340", {"start": v(-1.44, -12.08) * mm, "end": v(-1.3, -12.44) * mm});
            skLineSegment(sketch, "E341", {"start": v(-1.3, -12.44) * mm, "end": v(-0.9, -12.5) * mm});
            skLineSegment(sketch, "E342", {"start": v(-0.9, -12.5) * mm, "end": v(-0.5, -12.5) * mm});
            skLineSegment(sketch, "E343", {"start": v(-0.5, -12.5) * mm, "end": v(-0.3, -12.16) * mm});
            skLineSegment(sketch, "E344", {"start": v(-0.3, -12.16) * mm, "end": v(-0.14, -11.77) * mm});
            skLineSegment(sketch, "E345", {"start": v(-0.14, -11.77) * mm, "end": v(-0.03, -11.46) * mm});
            skLineSegment(sketch, "E346", {"start": v(-0.03, -11.46) * mm, "end": v(0.02, -11.22) * mm});
            skLineSegment(sketch, "E347", {"start": v(0.02, -11.22) * mm, "end": v(0.04, -11.08) * mm});
            skLineSegment(sketch, "E348", {"start": v(0.04, -11.08) * mm, "end": v(0.05, -10.82) * mm});
            skLineSegment(sketch, "E349", {"start": v(0.05, -10.82) * mm, "end": v(0.1, -10.61) * mm});
            skLineSegment(sketch, "E350", {"start": v(0.1, -10.61) * mm, "end": v(0.19, -10.51) * mm});
            skLineSegment(sketch, "E351", {"start": v(0.19, -10.51) * mm, "end": v(1.15, -10.45) * mm});
            skLineSegment(sketch, "E352", {"start": v(1.15, -10.45) * mm, "end": v(1.24, -10.54) * mm});
            skLineSegment(sketch, "E353", {"start": v(1.24, -10.54) * mm, "end": v(1.32, -10.73) * mm});
            skLineSegment(sketch, "E354", {"start": v(1.32, -10.73) * mm, "end": v(1.37, -10.98) * mm});
            skLineSegment(sketch, "E355", {"start": v(1.37, -10.98) * mm, "end": v(1.41, -11.13) * mm});
            skLineSegment(sketch, "E356", {"start": v(1.41, -11.13) * mm, "end": v(1.5, -11.35) * mm});
            skLineSegment(sketch, "E357", {"start": v(1.5, -11.35) * mm, "end": v(1.65, -11.65) * mm});
            skLineSegment(sketch, "E358", {"start": v(1.65, -11.65) * mm, "end": v(1.87, -12.01) * mm});
            skLineSegment(sketch, "E359", {"start": v(1.87, -12.01) * mm, "end": v(2.1, -12.32) * mm});
            skLineSegment(sketch, "E360", {"start": v(2.1, -12.32) * mm, "end": v(2.5, -12.27) * mm});
            skLineSegment(sketch, "E361", {"start": v(2.5, -12.27) * mm, "end": v(2.9, -12.16) * mm});
            skLineSegment(sketch, "E362", {"start": v(2.9, -12.16) * mm, "end": v(2.98, -11.78) * mm});
            skLineSegment(sketch, "E363", {"start": v(2.98, -11.78) * mm, "end": v(3.04, -11.36) * mm});
            skLineSegment(sketch, "E364", {"start": v(3.04, -11.36) * mm, "end": v(3.06, -11.03) * mm});
            skLineSegment(sketch, "E365", {"start": v(3.06, -11.03) * mm, "end": v(3.05, -10.79) * mm});
            skLineSegment(sketch, "E366", {"start": v(3.05, -10.79) * mm, "end": v(3.03, -10.64) * mm});
            skLineSegment(sketch, "E367", {"start": v(3.03, -10.64) * mm, "end": v(2.97, -10.39) * mm});
            skLineSegment(sketch, "E368", {"start": v(2.97, -10.39) * mm, "end": v(2.97, -10.18) * mm});
            skLineSegment(sketch, "E369", {"start": v(2.97, -10.18) * mm, "end": v(3.02, -10.06) * mm});
            skLineSegment(sketch, "E370", {"start": v(3.02, -10.06) * mm, "end": v(3.92, -9.74) * mm});
            skLineSegment(sketch, "E371", {"start": v(3.92, -9.74) * mm, "end": v(4.04, -9.8) * mm});
            skLineSegment(sketch, "E372", {"start": v(4.04, -9.8) * mm, "end": v(4.17, -9.96) * mm});
            skLineSegment(sketch, "E373", {"start": v(4.17, -9.96) * mm, "end": v(4.28, -10.2) * mm});
            skLineSegment(sketch, "E374", {"start": v(4.28, -10.2) * mm, "end": v(4.36, -10.32) * mm});
            skLineSegment(sketch, "E375", {"start": v(4.36, -10.32) * mm, "end": v(4.5, -10.51) * mm});
            skLineSegment(sketch, "E376", {"start": v(4.5, -10.51) * mm, "end": v(4.73, -10.76) * mm});
            skLineSegment(sketch, "E377", {"start": v(4.73, -10.76) * mm, "end": v(5.04, -11.05) * mm});
            skLineSegment(sketch, "E378", {"start": v(5.04, -11.05) * mm, "end": v(5.34, -11.29) * mm});
            skLineSegment(sketch, "E379", {"start": v(5.34, -11.29) * mm, "end": v(5.72, -11.12) * mm});
            skLineSegment(sketch, "E380", {"start": v(5.72, -11.12) * mm, "end": v(6.06, -10.91) * mm});
            skLineSegment(sketch, "E381", {"start": v(6.06, -10.91) * mm, "end": v(6.05, -10.53) * mm});
            skLineSegment(sketch, "E382", {"start": v(6.05, -10.53) * mm, "end": v(6, -10.1) * mm});
            skLineSegment(sketch, "E383", {"start": v(6, -10.1) * mm, "end": v(5.92, -9.78) * mm});
            skLineSegment(sketch, "E384", {"start": v(5.92, -9.78) * mm, "end": v(5.84, -9.55) * mm});
            skLineSegment(sketch, "E385", {"start": v(5.84, -9.55) * mm, "end": v(5.78, -9.42) * mm});
            skLineSegment(sketch, "E386", {"start": v(5.78, -9.42) * mm, "end": v(5.66, -9.19) * mm});
            skLineSegment(sketch, "E387", {"start": v(5.66, -9.19) * mm, "end": v(5.6, -8.99) * mm});
            skLineSegment(sketch, "E388", {"start": v(5.6, -8.99) * mm, "end": v(5.62, -8.86) * mm});
            skLineSegment(sketch, "E389", {"start": v(5.62, -8.86) * mm, "end": v(6.4, -8.3) * mm});
            skLineSegment(sketch, "E390", {"start": v(6.4, -8.3) * mm, "end": v(6.53, -8.33) * mm});
            skLineSegment(sketch, "E391", {"start": v(6.53, -8.33) * mm, "end": v(6.7, -8.46) * mm});
            skLineSegment(sketch, "E392", {"start": v(6.7, -8.46) * mm, "end": v(6.87, -8.65) * mm});
            skLineSegment(sketch, "E393", {"start": v(6.87, -8.65) * mm, "end": v(6.98, -8.75) * mm});
            skLineSegment(sketch, "E394", {"start": v(6.98, -8.75) * mm, "end": v(7.17, -8.9) * mm});
            skLineSegment(sketch, "E395", {"start": v(7.17, -8.9) * mm, "end": v(7.45, -9.07) * mm});
            skLineSegment(sketch, "E396", {"start": v(7.45, -9.07) * mm, "end": v(7.83, -9.27) * mm});
            skLineSegment(sketch, "E397", {"start": v(7.83, -9.27) * mm, "end": v(8.19, -9.41) * mm});
            skLineSegment(sketch, "E398", {"start": v(8.19, -9.41) * mm, "end": v(8.5, -9.16) * mm});
            skLineSegment(sketch, "E399", {"start": v(8.5, -9.16) * mm, "end": v(8.78, -8.86) * mm});
            skLineSegment(sketch, "E400", {"start": v(8.78, -8.86) * mm, "end": v(8.66, -8.5) * mm});
            skLineSegment(sketch, "E401", {"start": v(8.66, -8.5) * mm, "end": v(8.5, -8.1) * mm});
            skLineSegment(sketch, "E402", {"start": v(8.5, -8.1) * mm, "end": v(8.34, -7.81) * mm});
            skLineSegment(sketch, "E403", {"start": v(8.34, -7.81) * mm, "end": v(8.2, -7.6) * mm});
            skLineSegment(sketch, "E404", {"start": v(8.2, -7.6) * mm, "end": v(8.1, -7.5) * mm});
            skLineSegment(sketch, "E405", {"start": v(8.1, -7.5) * mm, "end": v(7.93, -7.3) * mm});
            skLineSegment(sketch, "E406", {"start": v(7.93, -7.3) * mm, "end": v(7.82, -7.13) * mm});
            skLineSegment(sketch, "E407", {"start": v(7.82, -7.13) * mm, "end": v(7.8, -7) * mm});
            skLineSegment(sketch, "E408", {"start": v(7.8, -7) * mm, "end": v(8.4, -6.26) * mm});
            skLineSegment(sketch, "E409", {"start": v(8.4, -6.26) * mm, "end": v(8.53, -6.25) * mm});
            skLineSegment(sketch, "E410", {"start": v(8.53, -6.25) * mm, "end": v(8.73, -6.32) * mm});
            skLineSegment(sketch, "E411", {"start": v(8.73, -6.32) * mm, "end": v(8.95, -6.46) * mm});
            skLineSegment(sketch, "E412", {"start": v(8.95, -6.46) * mm, "end": v(9.08, -6.53) * mm});
            skLineSegment(sketch, "E413", {"start": v(9.08, -6.53) * mm, "end": v(9.3, -6.62) * mm});
            skLineSegment(sketch, "E414", {"start": v(9.3, -6.62) * mm, "end": v(9.62, -6.71) * mm});
            skLineSegment(sketch, "E415", {"start": v(9.62, -6.71) * mm, "end": v(10.04, -6.8) * mm});
            skLineSegment(sketch, "E416", {"start": v(10.04, -6.8) * mm, "end": v(10.42, -6.84) * mm});
            skLineSegment(sketch, "E417", {"start": v(10.42, -6.84) * mm, "end": v(10.66, -6.5) * mm});
            skLineSegment(sketch, "E418", {"start": v(10.66, -6.5) * mm, "end": v(10.84, -6.15) * mm});
            skLineSegment(sketch, "E419", {"start": v(10.84, -6.15) * mm, "end": v(10.63, -5.83) * mm});
            skLineSegment(sketch, "E420", {"start": v(10.63, -5.83) * mm, "end": v(10.36, -5.5) * mm});
            skLineSegment(sketch, "E421", {"start": v(10.36, -5.5) * mm, "end": v(10.13, -5.26) * mm});
            skLineSegment(sketch, "E422", {"start": v(10.13, -5.26) * mm, "end": v(9.95, -5.1) * mm});
            skLineSegment(sketch, "E423", {"start": v(9.95, -5.1) * mm, "end": v(9.83, -5.02) * mm});
            skLineSegment(sketch, "E424", {"start": v(9.83, -5.02) * mm, "end": v(9.6, -4.89) * mm});
            skLineSegment(sketch, "E425", {"start": v(9.6, -4.89) * mm, "end": v(9.45, -4.75) * mm});
            skLineSegment(sketch, "E426", {"start": v(9.45, -4.75) * mm, "end": v(9.4, -4.63) * mm});
            skLineSegment(sketch, "E427", {"start": v(9.4, -4.63) * mm, "end": v(9.78, -3.74) * mm});
            skLineSegment(sketch, "E428", {"start": v(9.78, -3.74) * mm, "end": v(9.9, -3.7) * mm});
            skLineSegment(sketch, "E429", {"start": v(9.9, -3.7) * mm, "end": v(10.11, -3.72) * mm});
            skLineSegment(sketch, "E430", {"start": v(10.11, -3.72) * mm, "end": v(10.36, -3.8) * mm});
            skLineSegment(sketch, "E431", {"start": v(10.36, -3.8) * mm, "end": v(10.5, -3.82) * mm});
            skLineSegment(sketch, "E432", {"start": v(10.5, -3.82) * mm, "end": v(10.74, -3.85) * mm});
            skLineSegment(sketch, "E433", {"start": v(10.74, -3.85) * mm, "end": v(11.08, -3.86) * mm});
            skLineSegment(sketch, "E434", {"start": v(11.08, -3.86) * mm, "end": v(11.5, -3.83) * mm});
            skLineSegment(sketch, "E435", {"start": v(11.5, -3.83) * mm, "end": v(11.88, -3.76) * mm});
            skLineSegment(sketch, "E436", {"start": v(11.01, 2.2) * mm, "end": v(10.86, 1.92) * mm});
            skLineSegment(sketch, "E437", {"start": v(10.86, 1.92) * mm, "end": v(10.76, 1.6) * mm});
            skLineSegment(sketch, "E438", {"start": v(10.76, 1.6) * mm, "end": v(10.86, 1.43) * mm});
            skLineSegment(sketch, "E439", {"start": v(10.86, 1.43) * mm, "end": v(11.3, 0.96) * mm});
            skLineSegment(sketch, "E440", {"start": v(11.3, 0.96) * mm, "end": v(11.6, 0.76) * mm});
            skLineSegment(sketch, "E441", {"start": v(11.6, 0.76) * mm, "end": v(11.72, 0.72) * mm});
            skLineSegment(sketch, "E442", {"start": v(11.72, 0.72) * mm, "end": v(12.2, 0.7) * mm});
            skLineSegment(sketch, "E443", {"start": v(12.2, 0.7) * mm, "end": v(12.5, 0.48) * mm});
            skLineSegment(sketch, "E444", {"start": v(12.5, 0.48) * mm, "end": v(12.5, -0.48) * mm});
            skLineSegment(sketch, "E445", {"start": v(12.5, -0.48) * mm, "end": v(12.2, -0.7) * mm});
            skLineSegment(sketch, "E446", {"start": v(12.2, -0.7) * mm, "end": v(11.72, -0.72) * mm});
            skLineSegment(sketch, "E447", {"start": v(11.72, -0.72) * mm, "end": v(11.6, -0.76) * mm});
            skLineSegment(sketch, "E448", {"start": v(11.6, -0.76) * mm, "end": v(11.3, -0.96) * mm});
            skLineSegment(sketch, "E449", {"start": v(11.3, -0.96) * mm, "end": v(10.86, -1.43) * mm});
            skLineSegment(sketch, "E450", {"start": v(10.86, -1.43) * mm, "end": v(10.76, -1.6) * mm});
            skLineSegment(sketch, "E451", {"start": v(10.76, -1.6) * mm, "end": v(10.86, -1.92) * mm});
            skLineSegment(sketch, "E452", {"start": v(10.86, -1.92) * mm, "end": v(11.01, -2.2) * mm});
            skLineSegment(sketch, "E453", {"start": v(11.01, -2.2) * mm, "end": v(11.2, -2.27) * mm});
            skLineSegment(sketch, "E454", {"start": v(11.2, -2.27) * mm, "end": v(11.84, -2.3) * mm});
            skLineSegment(sketch, "E455", {"start": v(11.84, -2.3) * mm, "end": v(12.2, -2.2) * mm});
            skLineSegment(sketch, "E456", {"start": v(12.2, -2.2) * mm, "end": v(12.3, -2.16) * mm});
            skLineSegment(sketch, "E457", {"start": v(12.3, -2.16) * mm, "end": v(12.67, -1.82) * mm});
            skLineSegment(sketch, "E458", {"start": v(12.67, -1.82) * mm, "end": v(13.04, -1.77) * mm});
            skLineSegment(sketch, "E459", {"start": v(13.04, -1.77) * mm, "end": v(13.72, -2.45) * mm});
            skLineSegment(sketch, "E460", {"start": v(13.72, -2.45) * mm, "end": v(13.67, -2.82) * mm});
            skLineSegment(sketch, "E461", {"start": v(13.67, -2.82) * mm, "end": v(13.33, -3.18) * mm});
            skLineSegment(sketch, "E462", {"start": v(13.33, -3.18) * mm, "end": v(13.28, -3.28) * mm});
            skLineSegment(sketch, "E463", {"start": v(13.28, -3.28) * mm, "end": v(13.2, -3.64) * mm});
            skLineSegment(sketch, "E464", {"start": v(13.2, -3.64) * mm, "end": v(13.22, -4.28) * mm});
            skLineSegment(sketch, "E465", {"start": v(13.22, -4.28) * mm, "end": v(13.28, -4.48) * mm});
            skLineSegment(sketch, "E466", {"start": v(13.28, -4.48) * mm, "end": v(13.57, -4.63) * mm});
            skLineSegment(sketch, "E467", {"start": v(13.57, -4.63) * mm, "end": v(13.88, -4.73) * mm});
            skLineSegment(sketch, "E468", {"start": v(13.88, -4.73) * mm, "end": v(14.06, -4.63) * mm});
            skLineSegment(sketch, "E469", {"start": v(14.06, -4.63) * mm, "end": v(14.53, -4.2) * mm});
            skLineSegment(sketch, "E470", {"start": v(14.53, -4.2) * mm, "end": v(14.73, -3.88) * mm});
            skLineSegment(sketch, "E471", {"start": v(14.73, -3.88) * mm, "end": v(14.76, -3.77) * mm});
            skLineSegment(sketch, "E472", {"start": v(14.76, -3.77) * mm, "end": v(14.78, -3.28) * mm});
            skLineSegment(sketch, "E473", {"start": v(14.78, -3.28) * mm, "end": v(15, -2.99) * mm});
            skLineSegment(sketch, "E474", {"start": v(15, -2.99) * mm, "end": v(15.97, -2.99) * mm});
            skLineSegment(sketch, "E475", {"start": v(15.97, -2.99) * mm, "end": v(16.2, -3.28) * mm});
            skLineSegment(sketch, "E476", {"start": v(16.2, -3.28) * mm, "end": v(16.21, -3.77) * mm});
            skLineSegment(sketch, "E477", {"start": v(16.21, -3.77) * mm, "end": v(16.25, -3.88) * mm});
            skLineSegment(sketch, "E478", {"start": v(16.25, -3.88) * mm, "end": v(16.45, -4.2) * mm});
            skLineSegment(sketch, "E479", {"start": v(16.45, -4.2) * mm, "end": v(16.91, -4.63) * mm});
            skLineSegment(sketch, "E480", {"start": v(16.91, -4.63) * mm, "end": v(17.1, -4.73) * mm});
            skLineSegment(sketch, "E481", {"start": v(17.1, -4.73) * mm, "end": v(17.4, -4.63) * mm});
            skLineSegment(sketch, "E482", {"start": v(17.4, -4.63) * mm, "end": v(17.7, -4.48) * mm});
            skLineSegment(sketch, "E483", {"start": v(17.7, -4.48) * mm, "end": v(17.76, -4.28) * mm});
            skLineSegment(sketch, "E484", {"start": v(17.76, -4.28) * mm, "end": v(17.78, -3.64) * mm});
            skLineSegment(sketch, "E485", {"start": v(17.78, -3.64) * mm, "end": v(17.7, -3.28) * mm});
            skLineSegment(sketch, "E486", {"start": v(17.7, -3.28) * mm, "end": v(17.64, -3.18) * mm});
            skLineSegment(sketch, "E487", {"start": v(17.64, -3.18) * mm, "end": v(17.3, -2.82) * mm});
            skLineSegment(sketch, "E488", {"start": v(17.3, -2.82) * mm, "end": v(17.26, -2.45) * mm});
            skLineSegment(sketch, "E489", {"start": v(17.26, -2.45) * mm, "end": v(17.94, -1.77) * mm});
            skLineSegment(sketch, "E490", {"start": v(17.94, -1.77) * mm, "end": v(18.3, -1.82) * mm});
            skLineSegment(sketch, "E491", {"start": v(18.3, -1.82) * mm, "end": v(18.67, -2.16) * mm});
            skLineSegment(sketch, "E492", {"start": v(18.67, -2.16) * mm, "end": v(18.77, -2.2) * mm});
            skLineSegment(sketch, "E493", {"start": v(18.77, -2.2) * mm, "end": v(19.13, -2.3) * mm});
            skLineSegment(sketch, "E494", {"start": v(19.13, -2.3) * mm, "end": v(19.77, -2.27) * mm});
            skLineSegment(sketch, "E495", {"start": v(19.77, -2.27) * mm, "end": v(19.96, -2.2) * mm});
            skLineSegment(sketch, "E496", {"start": v(19.96, -2.2) * mm, "end": v(20.12, -1.92) * mm});
            skLineSegment(sketch, "E497", {"start": v(20.12, -1.92) * mm, "end": v(20.21, -1.6) * mm});
            skLineSegment(sketch, "E498", {"start": v(20.21, -1.6) * mm, "end": v(20.12, -1.43) * mm});
            skLineSegment(sketch, "E499", {"start": v(20.12, -1.43) * mm, "end": v(19.69, -0.96) * mm});
            skLineSegment(sketch, "E500", {"start": v(19.69, -0.96) * mm, "end": v(19.37, -0.76) * mm});
            skLineSegment(sketch, "E501", {"start": v(19.37, -0.76) * mm, "end": v(19.26, -0.72) * mm});
            skLineSegment(sketch, "E502", {"start": v(19.26, -0.72) * mm, "end": v(18.77, -0.7) * mm});
            skLineSegment(sketch, "E503", {"start": v(18.77, -0.7) * mm, "end": v(18.48, -0.48) * mm});
            skLineSegment(sketch, "E504", {"start": v(18.48, -0.48) * mm, "end": v(18.48, 0.48) * mm});
            skLineSegment(sketch, "E505", {"start": v(18.48, 0.48) * mm, "end": v(18.77, 0.7) * mm});
            skLineSegment(sketch, "E506", {"start": v(18.77, 0.7) * mm, "end": v(19.26, 0.72) * mm});
            skLineSegment(sketch, "E507", {"start": v(19.26, 0.72) * mm, "end": v(19.37, 0.76) * mm});
            skLineSegment(sketch, "E508", {"start": v(19.37, 0.76) * mm, "end": v(19.69, 0.96) * mm});
            skLineSegment(sketch, "E509", {"start": v(19.69, 0.96) * mm, "end": v(20.12, 1.43) * mm});
            skLineSegment(sketch, "E510", {"start": v(20.12, 1.43) * mm, "end": v(20.21, 1.6) * mm});
            skLineSegment(sketch, "E511", {"start": v(20.21, 1.6) * mm, "end": v(20.12, 1.92) * mm});
            skLineSegment(sketch, "E512", {"start": v(20.12, 1.92) * mm, "end": v(19.96, 2.2) * mm});
            skLineSegment(sketch, "E513", {"start": v(19.96, 2.2) * mm, "end": v(19.77, 2.27) * mm});
            skLineSegment(sketch, "E514", {"start": v(19.77, 2.27) * mm, "end": v(19.13, 2.3) * mm});
            skLineSegment(sketch, "E515", {"start": v(19.13, 2.3) * mm, "end": v(18.77, 2.2) * mm});
            skLineSegment(sketch, "E516", {"start": v(18.77, 2.2) * mm, "end": v(18.67, 2.16) * mm});
            skLineSegment(sketch, "E517", {"start": v(18.67, 2.16) * mm, "end": v(18.3, 1.82) * mm});
            skLineSegment(sketch, "E518", {"start": v(18.3, 1.82) * mm, "end": v(17.94, 1.77) * mm});
            skLineSegment(sketch, "E519", {"start": v(17.94, 1.77) * mm, "end": v(17.26, 2.45) * mm});
            skLineSegment(sketch, "E520", {"start": v(17.26, 2.45) * mm, "end": v(17.3, 2.82) * mm});
            skLineSegment(sketch, "E521", {"start": v(17.3, 2.82) * mm, "end": v(17.64, 3.18) * mm});
            skLineSegment(sketch, "E522", {"start": v(17.64, 3.18) * mm, "end": v(17.7, 3.28) * mm});
            skLineSegment(sketch, "E523", {"start": v(17.7, 3.28) * mm, "end": v(17.78, 3.64) * mm});
            skLineSegment(sketch, "E524", {"start": v(17.78, 3.64) * mm, "end": v(17.76, 4.28) * mm});
            skLineSegment(sketch, "E525", {"start": v(17.76, 4.28) * mm, "end": v(17.7, 4.48) * mm});
            skLineSegment(sketch, "E526", {"start": v(17.7, 4.48) * mm, "end": v(17.4, 4.63) * mm});
            skLineSegment(sketch, "E527", {"start": v(17.4, 4.63) * mm, "end": v(17.1, 4.73) * mm});
            skLineSegment(sketch, "E528", {"start": v(17.1, 4.73) * mm, "end": v(16.91, 4.63) * mm});
            skLineSegment(sketch, "E529", {"start": v(16.91, 4.63) * mm, "end": v(16.45, 4.2) * mm});
            skLineSegment(sketch, "E530", {"start": v(16.45, 4.2) * mm, "end": v(16.25, 3.88) * mm});
            skLineSegment(sketch, "E531", {"start": v(16.25, 3.88) * mm, "end": v(16.21, 3.77) * mm});
            skLineSegment(sketch, "E532", {"start": v(16.21, 3.77) * mm, "end": v(16.2, 3.28) * mm});
            skLineSegment(sketch, "E533", {"start": v(16.2, 3.28) * mm, "end": v(15.97, 2.99) * mm});
            skLineSegment(sketch, "E534", {"start": v(15.97, 2.99) * mm, "end": v(15, 2.99) * mm});
            skLineSegment(sketch, "E535", {"start": v(15, 2.99) * mm, "end": v(14.78, 3.28) * mm});
            skLineSegment(sketch, "E536", {"start": v(14.78, 3.28) * mm, "end": v(14.76, 3.77) * mm});
            skLineSegment(sketch, "E537", {"start": v(14.76, 3.77) * mm, "end": v(14.73, 3.88) * mm});
            skLineSegment(sketch, "E538", {"start": v(14.73, 3.88) * mm, "end": v(14.53, 4.2) * mm});
            skLineSegment(sketch, "E539", {"start": v(14.53, 4.2) * mm, "end": v(14.06, 4.63) * mm});
            skLineSegment(sketch, "E540", {"start": v(14.06, 4.63) * mm, "end": v(13.88, 4.73) * mm});
            skLineSegment(sketch, "E541", {"start": v(13.88, 4.73) * mm, "end": v(13.57, 4.63) * mm});
            skLineSegment(sketch, "E542", {"start": v(13.57, 4.63) * mm, "end": v(13.28, 4.48) * mm});
            skLineSegment(sketch, "E543", {"start": v(13.28, 4.48) * mm, "end": v(13.22, 4.28) * mm});
            skLineSegment(sketch, "E544", {"start": v(13.22, 4.28) * mm, "end": v(13.2, 3.64) * mm});
            skLineSegment(sketch, "E545", {"start": v(13.2, 3.64) * mm, "end": v(13.28, 3.28) * mm});
            skLineSegment(sketch, "E546", {"start": v(13.28, 3.28) * mm, "end": v(13.33, 3.18) * mm});
            skLineSegment(sketch, "E547", {"start": v(13.33, 3.18) * mm, "end": v(13.67, 2.82) * mm});
            skLineSegment(sketch, "E548", {"start": v(13.67, 2.82) * mm, "end": v(13.72, 2.45) * mm});
            skLineSegment(sketch, "E549", {"start": v(13.72, 2.45) * mm, "end": v(13.04, 1.77) * mm});
            skLineSegment(sketch, "E550", {"start": v(13.04, 1.77) * mm, "end": v(12.67, 1.82) * mm});
            skLineSegment(sketch, "E551", {"start": v(12.67, 1.82) * mm, "end": v(12.3, 2.16) * mm});
            skLineSegment(sketch, "E552", {"start": v(12.3, 2.16) * mm, "end": v(12.2, 2.2) * mm});
            skLineSegment(sketch, "E553", {"start": v(12.2, 2.2) * mm, "end": v(11.84, 2.3) * mm});
            skLineSegment(sketch, "E554", {"start": v(11.84, 2.3) * mm, "end": v(11.2, 2.27) * mm});
            skLineSegment(sketch, "E555", {"start": v(11.2, 2.27) * mm, "end": v(11.01, 2.2) * mm});
            skLineSegment(sketch, "E556", {"start": v(15.04, 0.65) * mm, "end": v(15.19, 0.73) * mm});
            skLineSegment(sketch, "E557", {"start": v(15.19, 0.73) * mm, "end": v(15.35, 0.77) * mm});
            skLineSegment(sketch, "E558", {"start": v(15.35, 0.77) * mm, "end": v(15.5, 0.79) * mm});
            skLineSegment(sketch, "E559", {"start": v(15.5, 0.79) * mm, "end": v(15.67, 0.77) * mm});
            skLineSegment(sketch, "E560", {"start": v(15.67, 0.77) * mm, "end": v(15.83, 0.71) * mm});
            skLineSegment(sketch, "E561", {"start": v(15.83, 0.71) * mm, "end": v(15.97, 0.62) * mm});
            skLineSegment(sketch, "E562", {"start": v(15.97, 0.62) * mm, "end": v(16.09, 0.51) * mm});
            skLineSegment(sketch, "E563", {"start": v(16.09, 0.51) * mm, "end": v(16.18, 0.38) * mm});
            skLineSegment(sketch, "E564", {"start": v(16.18, 0.38) * mm, "end": v(16.24, 0.22) * mm});
            skLineSegment(sketch, "E565", {"start": v(16.24, 0.22) * mm, "end": v(16.27, 0.06) * mm});
            skLineSegment(sketch, "E566", {"start": v(16.27, 0.06) * mm, "end": v(16.27, -0.1) * mm});
            skLineSegment(sketch, "E567", {"start": v(16.27, -0.1) * mm, "end": v(16.23, -0.26) * mm});
            skLineSegment(sketch, "E568", {"start": v(16.23, -0.26) * mm, "end": v(16.16, -0.41) * mm});
            skLineSegment(sketch, "E569", {"start": v(16.16, -0.41) * mm, "end": v(16.06, -0.54) * mm});
            skLineSegment(sketch, "E570", {"start": v(16.06, -0.54) * mm, "end": v(15.93, -0.65) * mm});
            skLineSegment(sketch, "E571", {"start": v(15.93, -0.65) * mm, "end": v(15.79, -0.73) * mm});
            skLineSegment(sketch, "E572", {"start": v(15.79, -0.73) * mm, "end": v(15.63, -0.77) * mm});
            skLineSegment(sketch, "E573", {"start": v(15.63, -0.77) * mm, "end": v(15.47, -0.79) * mm});
            skLineSegment(sketch, "E574", {"start": v(15.47, -0.79) * mm, "end": v(15.3, -0.77) * mm});
            skLineSegment(sketch, "E575", {"start": v(15.3, -0.77) * mm, "end": v(15.15, -0.71) * mm});
            skLineSegment(sketch, "E576", {"start": v(15.15, -0.71) * mm, "end": v(15, -0.62) * mm});
            skLineSegment(sketch, "E577", {"start": v(15, -0.62) * mm, "end": v(14.89, -0.51) * mm});
            skLineSegment(sketch, "E578", {"start": v(14.89, -0.51) * mm, "end": v(14.8, -0.38) * mm});
            skLineSegment(sketch, "E579", {"start": v(14.8, -0.38) * mm, "end": v(14.73, -0.22) * mm});
            skLineSegment(sketch, "E580", {"start": v(14.73, -0.22) * mm, "end": v(14.7, -0.06) * mm});
            skLineSegment(sketch, "E581", {"start": v(14.7, -0.06) * mm, "end": v(14.7, 0.1) * mm});
            skLineSegment(sketch, "E582", {"start": v(14.7, 0.1) * mm, "end": v(14.75, 0.26) * mm});
            skLineSegment(sketch, "E583", {"start": v(14.75, 0.26) * mm, "end": v(14.82, 0.41) * mm});
            skLineSegment(sketch, "E584", {"start": v(14.82, 0.41) * mm, "end": v(14.92, 0.54) * mm});
            skLineSegment(sketch, "E585", {"start": v(14.92, 0.54) * mm, "end": v(15.04, 0.65) * mm});
            skCircle(sketch, "E586", {"center": v(0, 0) * mm, "radius": 2 * mm});
            skLineSegment(sketch, "E587", {"start": v(12.02, 3.38) * mm, "end": v(12.1, 2.98) * mm});
            skSolve(sketch);
        }
        {
            var Q0;
            Q0=makeQuery(id+"F0.imprint","IMPRINT",FACE,{"disambiguationData":[TD([[makeQuery(id+"F0.imprint","IMPRINT",EDGE,{"derivedFrom":sQuery(id+"F0.wireOp",EDGE,"E0")}),1.0]])]});
            extrude(context, id + "F1", {"entities" : qUnion([Q0]), "offsetDistance" : 25 * mm, "depth" : 7 * mm});
        }
    });
